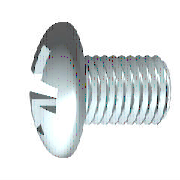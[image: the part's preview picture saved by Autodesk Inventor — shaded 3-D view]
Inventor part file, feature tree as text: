
AUTODESK INVENTOR PART (.ipt)
format: ipt  version: 2020 (Build 240168000, 168)  size: 270,848 bytes
history: native  units: mm (DEFAULTED — no unit token found)
features: other x2, plane x2, extrude x1
ambient origin geometry x7: Origin, YZ Plane, XZ Plane, X Axis, Y Axis, Z Axis, Center Point
bodies: Solid1 (feature_tree)
feature tree (5):
  other  "Базовый элемент"
  plane  "Work Plane1"
  extrude  "Паз"  Depth=2.0mm
  other  "Вырез"
  plane  "Work Plane3"
